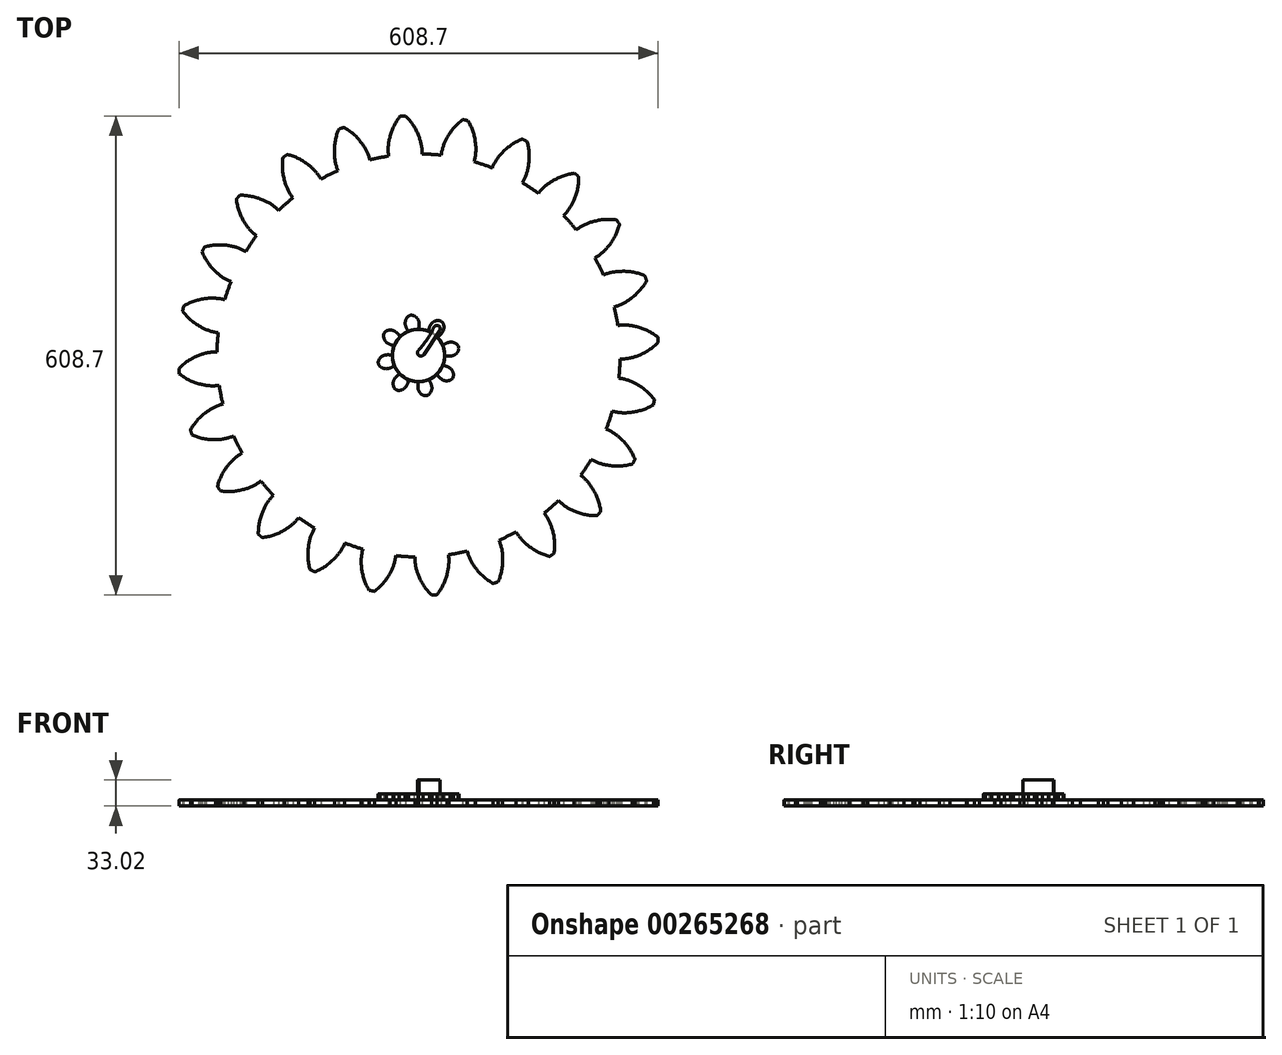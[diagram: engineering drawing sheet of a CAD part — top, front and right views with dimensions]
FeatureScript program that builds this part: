
annotation { "Feature Type Name" : "Feature", "Feature Type Description" : "" }
export const myFeature = defineFeature(function(context is Context, id is Id, definition is map)
    precondition{}
    {
        {
            var Q0;
            Q0=qCreatedBy(makeId("Top.planeOp"),FACE);
            var sketch = newSketch(context, id + "F0", { "sketchPlane" : qUnion([Q0])});
            skCircle(sketch, "E0", {"center": v(0, 0) * mm, "radius": 33.25 * mm});
            skCircle(sketch, "E1", {"center": v(0, 0) * mm, "radius": 44.32 * mm, "construction": true});
            skCircle(sketch, "E2", {"center": v(0, 0) * mm, "radius": 50.8 * mm, "construction": true});
            skLineSegment(sketch, "E3", {"start": v(0, 0) * mm, "end": v(0, 420.14) * mm, "construction": true});
            skLineSegment(sketch, "E4", {"start": v(0, 0) * mm, "end": v(-79.68, 400.58) * mm, "construction": true});
            skLineSegment(sketch, "E5", {"start": v(0, 44.32) * mm, "end": v(-381.83, 44.32) * mm, "construction": true});
            skLineSegment(sketch, "E6", {"start": v(0, 44.32) * mm, "end": v(-397.99, -100.53) * mm, "construction": true});
            skCircle(sketch, "E7", {"center": v(0, 0) * mm, "radius": 41.65 * mm, "construction": true});
            skCircle(sketch, "E8", {"center": v(0, 44.32) * mm, "radius": 11.08 * mm, "construction": true});
            skCircle(sketch, "E9", {"center": v(-10.35, 40.34) * mm, "radius": 69.82 * mm, "construction": true});
            skCircle(sketch, "E10", {"center": v(-10.35, 40.34) * mm, "radius": 11.08 * mm, "construction": true});
            skArc(sketch, "E11", {"start": v(0, 44.32) * mm, "mid": v(-2.33, 47.95) * mm, "end": v(-5.83, 50.46) * mm});
            skArc(sketch, "E12", {"start": v(0, 33.24) * mm, "mid": v(0.9, 38.78) * mm, "end": v(0, 44.32) * mm});
            skArc(sketch, "E13.MirrorCS", {"start": v(-12.72, 30.7) * mm, "mid": v(-15.67, 35.49) * mm, "end": v(-16.96, 40.95) * mm});
            skArc(sketch, "E14.MirrorCS", {"start": v(-16.96, 40.95) * mm, "mid": v(-16.2, 45.2) * mm, "end": v(-13.93, 48.85) * mm});
            skArc(sketch, "E15", {"start": v(-5.83, 50.46) * mm, "mid": v(-10.15, 51.04) * mm, "end": v(-13.93, 48.85) * mm});
            skSolve(sketch);
        }
        {
            var Q0;
            Q0=qSketchRegion(id+"F0",true);
            extrude(context, id + "F1", {"entities" : qUnion([Q0]), "depth" : 7.62 * mm});
        }
        {
            var Q0;
            Q0=makeQuery(id+"F1.opExtrude","SWEPT_BODY",BODY,{"disambiguationData":[OSD([sQuery(id+"F0.wireOp",EDGE,"E0"),sQuery(id+"F0.wireOp",EDGE,"91NiUCr4-yXFt-oEsC-2t8w-iLQuIMEs0WGp"),sQuery(id+"F0.wireOp",EDGE,"2eccd6a7-b62e-4e30-96b3-c5b5e07e5a5b0.MirrorCS"),sQuery(id+"F0.wireOp",EDGE,"SwGH1OBa-uFWg-PKz4-vmGh-Pag9Jd44Z9b1")])]});
            var Q1;
            Q1=makeQuery(id+"F1.opExtrude","SWEPT_FACE",FACE,{"disambiguationData":[OSD([sQuery(id+"F0.wireOp",EDGE,"E0")])]});
            circularPattern(context, id + "F2", {"entities" : qUnion([Q0]), "axis" : qUnion([Q1]), "angle" : 360 * degree, "instanceCount" : 8, "equalSpace" : true});
        }
        {
            var Q0;
            Q0=qCreatedBy(makeId("Top.planeOp"),FACE);
            var sketch = newSketch(context, id + "F3", { "sketchPlane" : qUnion([Q0])});
            skLineSegment(sketch, "E16", {"start": v(0, 0) * mm, "end": v(85.76, 128.36) * mm, "construction": true});
            skLineSegment(sketch, "E17.bottom", {"start": v(4.22, -2.82) * mm, "end": v(29.62, 35.2) * mm});
            skLineSegment(sketch, "E17.top", {"start": v(0, 0) * mm, "end": v(25.4, 38.01) * mm});
            skLineSegment(sketch, "E17.left", {"start": v(4.22, -2.82) * mm, "end": v(0, 0) * mm});
            skLineSegment(sketch, "E17.right", {"start": v(29.62, 35.2) * mm, "end": v(25.4, 38.01) * mm});
            skLineSegment(sketch, "E18.left", {"start": v(-4.22, 2.82) * mm, "end": v(0, 0) * mm});
            skLineSegment(sketch, "E18.right", {"start": v(21.18, 40.84) * mm, "end": v(25.4, 38.01) * mm});
            skArc(sketch, "E19", {"start": v(-4.22, 2.82) * mm, "mid": v(10.92, 20.2) * mm, "end": v(21.18, 40.84) * mm});
            skSolve(sketch);
        }
        {
            var Q0;
            Q0 = qSketchRegion(id + "F3", true);
            extrude(context, id + "F4", {"entities" : qUnion([Q0]), "depth" : 25.4 * mm});
        }
        {
            var Q0;
            Q0=makeQuery(id+"F4.opExtrude","SWEPT_EDGE",EDGE,{"disambiguationData":[OSD([sQuery(id+"F3.wireOp",EDGE,"E17.bottom"),sQuery(id+"F3.wireOp",EDGE,"E17.right")])]});
            var Q1;
            Q1=makeQuery(id+"F4.opExtrude","SWEPT_EDGE",EDGE,{"disambiguationData":[OSD([sQuery(id+"F3.wireOp",EDGE,"E17.bottom"),sQuery(id+"F3.wireOp",EDGE,"E17.left")])]});
            var Q2;
            Q2=makeQuery(id+"F4.opExtrude","SWEPT_EDGE",EDGE,{"disambiguationData":[OSD([sQuery(id+"F3.wireOp",EDGE,"E18.left"),sQuery(id+"F3.wireOp",EDGE,"E19")])]});
            var Q3;
            Q3=makeQuery(id+"F4.opExtrude","SWEPT_EDGE",EDGE,{"disambiguationData":[OSD([sQuery(id+"F3.wireOp",EDGE,"E18.right"),sQuery(id+"F3.wireOp",EDGE,"E19")])]});
            fillet(context, id + "F5", {"entities" : qUnion([Q0, Q1, Q2, Q3]), "radius" : 5.08 * mm, "tangentPropagation" : true, "allowEdgeOverflow" : false});
        }
        {
            var Q0;
            Q0=qCreatedBy(makeId("Top.planeOp"),FACE);
            var sketch = newSketch(context, id + "F6", { "sketchPlane" : qUnion([Q0])});
            skCircle(sketch, "E20", {"center": v(0, 0) * mm, "radius": 256.02 * mm});
            skCircle(sketch, "E21", {"center": v(0, 0) * mm, "radius": 279.3 * mm, "construction": true});
            skCircle(sketch, "E22", {"center": v(0, 0) * mm, "radius": 304.8 * mm, "construction": true});
            skLineSegment(sketch, "E23", {"start": v(0, 0) * mm, "end": v(0, 185.17) * mm, "construction": true});
            skLineSegment(sketch, "E24", {"start": v(0, 0) * mm, "end": v(-26.71, 407.56) * mm, "construction": true});
            skLineSegment(sketch, "E25", {"start": v(0, 279.3) * mm, "end": v(-381.83, 279.3) * mm, "construction": true});
            skLineSegment(sketch, "E26", {"start": v(0, 279.3) * mm, "end": v(-397.99, 134.44) * mm, "construction": true});
            skCircle(sketch, "E27", {"center": v(0, 0) * mm, "radius": 262.45 * mm, "construction": true});
            skCircle(sketch, "E28", {"center": v(0, 279.3) * mm, "radius": 69.82 * mm, "construction": true});
            skCircle(sketch, "E29", {"center": v(-65.17, 254.23) * mm, "radius": 69.82 * mm, "construction": true});
            skArc(sketch, "E30", {"start": v(-16.55, 304.35) * mm, "mid": v(-19.94, 304.2) * mm, "end": v(-23.32, 303.9) * mm});
            skArc(sketch, "E31", {"start": v(0, 279.3) * mm, "mid": v(-6.88, 292.75) * mm, "end": v(-16.55, 304.35) * mm});
            skArc(sketch, "E32.MirrorCS", {"start": v(-36.46, 276.9) * mm, "mid": v(-31.4, 291.14) * mm, "end": v(-23.32, 303.9) * mm});
            skArc(sketch, "E33", {"start": v(-36.46, 276.9) * mm, "mid": v(-38.45, 265.13) * mm, "end": v(-38, 253.19) * mm});
            skArc(sketch, "E34.MirrorCS", {"start": v(0, 279.3) * mm, "mid": v(3.51, 267.88) * mm, "end": v(4.63, 255.98) * mm});
            skSolve(sketch);
        }
        {
            var Q0;
            Q0 = qSketchRegion(id + "F6", true);
            extrude(context, id + "F7", {"entities" : qUnion([Q0]), "depth" : 7.62 * mm});
        }
        {
            var Q0;
            Q0=makeQuery(id+"F7.opExtrude","SWEPT_BODY",BODY,{"disambiguationData":[OSD([sQuery(id+"F6.wireOp",EDGE,"E20"),sQuery(id+"F6.wireOp",EDGE,"E30"),sQuery(id+"F6.wireOp",EDGE,"E31"),sQuery(id+"F6.wireOp",EDGE,"E32.MirrorCS"),sQuery(id+"F6.wireOp",EDGE,"E33"),sQuery(id+"F6.wireOp",EDGE,"E34.MirrorCS")])]});
            var Q1;
            Q1=makeQuery(id+"F7.opExtrude","SWEPT_FACE",FACE,{"disambiguationData":[OSD([sQuery(id+"F6.wireOp",EDGE,"E20")])]});
            circularPattern(context, id + "F8", {"entities" : qUnion([Q0]), "axis" : qUnion([Q1]), "angle" : 360 * degree, "instanceCount" : 24, "equalSpace" : true});
        }
        {
            var Q0;
            Q0=makeQuery(id+"F7.opExtrude","SWEPT_BODY",BODY,{"disambiguationData":[OSD([sQuery(id+"F6.wireOp",EDGE,"E20"),sQuery(id+"F6.wireOp",EDGE,"E30"),sQuery(id+"F6.wireOp",EDGE,"E31"),sQuery(id+"F6.wireOp",EDGE,"E32.MirrorCS"),sQuery(id+"F6.wireOp",EDGE,"E33"),sQuery(id+"F6.wireOp",EDGE,"E34.MirrorCS")])]});
            var Q1;
            Q1=makeQuery(id+"F8.opPattern","COPY",BODY,{"derivedFrom":makeQuery(id+"F7.opExtrude","SWEPT_BODY",BODY,{"disambiguationData":[OSD([sQuery(id+"F6.wireOp",EDGE,"E20"),sQuery(id+"F6.wireOp",EDGE,"E30"),sQuery(id+"F6.wireOp",EDGE,"E31"),sQuery(id+"F6.wireOp",EDGE,"E32.MirrorCS"),sQuery(id+"F6.wireOp",EDGE,"E33"),sQuery(id+"F6.wireOp",EDGE,"E34.MirrorCS")])]}),"instanceName":"1"});
            var Q2;
            Q2=makeQuery(id+"F8.opPattern","COPY",BODY,{"derivedFrom":makeQuery(id+"F7.opExtrude","SWEPT_BODY",BODY,{"disambiguationData":[OSD([sQuery(id+"F6.wireOp",EDGE,"E20"),sQuery(id+"F6.wireOp",EDGE,"E30"),sQuery(id+"F6.wireOp",EDGE,"E31"),sQuery(id+"F6.wireOp",EDGE,"E32.MirrorCS"),sQuery(id+"F6.wireOp",EDGE,"E33"),sQuery(id+"F6.wireOp",EDGE,"E34.MirrorCS")])]}),"instanceName":"2"});
            var Q3;
            Q3=makeQuery(id+"F8.opPattern","COPY",BODY,{"derivedFrom":makeQuery(id+"F7.opExtrude","SWEPT_BODY",BODY,{"disambiguationData":[OSD([sQuery(id+"F6.wireOp",EDGE,"E20"),sQuery(id+"F6.wireOp",EDGE,"E30"),sQuery(id+"F6.wireOp",EDGE,"E31"),sQuery(id+"F6.wireOp",EDGE,"E32.MirrorCS"),sQuery(id+"F6.wireOp",EDGE,"E33"),sQuery(id+"F6.wireOp",EDGE,"E34.MirrorCS")])]}),"instanceName":"3"});
            var Q4;
            Q4=makeQuery(id+"F8.opPattern","COPY",BODY,{"derivedFrom":makeQuery(id+"F7.opExtrude","SWEPT_BODY",BODY,{"disambiguationData":[OSD([sQuery(id+"F6.wireOp",EDGE,"E20"),sQuery(id+"F6.wireOp",EDGE,"E30"),sQuery(id+"F6.wireOp",EDGE,"E31"),sQuery(id+"F6.wireOp",EDGE,"E32.MirrorCS"),sQuery(id+"F6.wireOp",EDGE,"E33"),sQuery(id+"F6.wireOp",EDGE,"E34.MirrorCS")])]}),"instanceName":"4"});
            var Q5;
            Q5=makeQuery(id+"F8.opPattern","COPY",BODY,{"derivedFrom":makeQuery(id+"F7.opExtrude","SWEPT_BODY",BODY,{"disambiguationData":[OSD([sQuery(id+"F6.wireOp",EDGE,"E20"),sQuery(id+"F6.wireOp",EDGE,"E30"),sQuery(id+"F6.wireOp",EDGE,"E31"),sQuery(id+"F6.wireOp",EDGE,"E32.MirrorCS"),sQuery(id+"F6.wireOp",EDGE,"E33"),sQuery(id+"F6.wireOp",EDGE,"E34.MirrorCS")])]}),"instanceName":"5"});
            var Q6;
            Q6=makeQuery(id+"F8.opPattern","COPY",BODY,{"derivedFrom":makeQuery(id+"F7.opExtrude","SWEPT_BODY",BODY,{"disambiguationData":[OSD([sQuery(id+"F6.wireOp",EDGE,"E20"),sQuery(id+"F6.wireOp",EDGE,"E30"),sQuery(id+"F6.wireOp",EDGE,"E31"),sQuery(id+"F6.wireOp",EDGE,"E32.MirrorCS"),sQuery(id+"F6.wireOp",EDGE,"E33"),sQuery(id+"F6.wireOp",EDGE,"E34.MirrorCS")])]}),"instanceName":"6"});
            var Q7;
            Q7=makeQuery(id+"F8.opPattern","COPY",BODY,{"derivedFrom":makeQuery(id+"F7.opExtrude","SWEPT_BODY",BODY,{"disambiguationData":[OSD([sQuery(id+"F6.wireOp",EDGE,"E20"),sQuery(id+"F6.wireOp",EDGE,"E30"),sQuery(id+"F6.wireOp",EDGE,"E31"),sQuery(id+"F6.wireOp",EDGE,"E32.MirrorCS"),sQuery(id+"F6.wireOp",EDGE,"E33"),sQuery(id+"F6.wireOp",EDGE,"E34.MirrorCS")])]}),"instanceName":"7"});
            var Q8;
            Q8=makeQuery(id+"F8.opPattern","COPY",BODY,{"derivedFrom":makeQuery(id+"F7.opExtrude","SWEPT_BODY",BODY,{"disambiguationData":[OSD([sQuery(id+"F6.wireOp",EDGE,"E20"),sQuery(id+"F6.wireOp",EDGE,"E30"),sQuery(id+"F6.wireOp",EDGE,"E31"),sQuery(id+"F6.wireOp",EDGE,"E32.MirrorCS"),sQuery(id+"F6.wireOp",EDGE,"E33"),sQuery(id+"F6.wireOp",EDGE,"E34.MirrorCS")])]}),"instanceName":"8"});
            var Q9;
            Q9=makeQuery(id+"F8.opPattern","COPY",BODY,{"derivedFrom":makeQuery(id+"F7.opExtrude","SWEPT_BODY",BODY,{"disambiguationData":[OSD([sQuery(id+"F6.wireOp",EDGE,"E20"),sQuery(id+"F6.wireOp",EDGE,"E30"),sQuery(id+"F6.wireOp",EDGE,"E31"),sQuery(id+"F6.wireOp",EDGE,"E32.MirrorCS"),sQuery(id+"F6.wireOp",EDGE,"E33"),sQuery(id+"F6.wireOp",EDGE,"E34.MirrorCS")])]}),"instanceName":"9"});
            var Q10;
            Q10=makeQuery(id+"F8.opPattern","COPY",BODY,{"derivedFrom":makeQuery(id+"F7.opExtrude","SWEPT_BODY",BODY,{"disambiguationData":[OSD([sQuery(id+"F6.wireOp",EDGE,"E20"),sQuery(id+"F6.wireOp",EDGE,"E30"),sQuery(id+"F6.wireOp",EDGE,"E31"),sQuery(id+"F6.wireOp",EDGE,"E32.MirrorCS"),sQuery(id+"F6.wireOp",EDGE,"E33"),sQuery(id+"F6.wireOp",EDGE,"E34.MirrorCS")])]}),"instanceName":"10"});
            var Q11;
            Q11=makeQuery(id+"F8.opPattern","COPY",BODY,{"derivedFrom":makeQuery(id+"F7.opExtrude","SWEPT_BODY",BODY,{"disambiguationData":[OSD([sQuery(id+"F6.wireOp",EDGE,"E20"),sQuery(id+"F6.wireOp",EDGE,"E30"),sQuery(id+"F6.wireOp",EDGE,"E31"),sQuery(id+"F6.wireOp",EDGE,"E32.MirrorCS"),sQuery(id+"F6.wireOp",EDGE,"E33"),sQuery(id+"F6.wireOp",EDGE,"E34.MirrorCS")])]}),"instanceName":"11"});
            var Q12;
            Q12=makeQuery(id+"F8.opPattern","COPY",BODY,{"derivedFrom":makeQuery(id+"F7.opExtrude","SWEPT_BODY",BODY,{"disambiguationData":[OSD([sQuery(id+"F6.wireOp",EDGE,"E20"),sQuery(id+"F6.wireOp",EDGE,"E30"),sQuery(id+"F6.wireOp",EDGE,"E31"),sQuery(id+"F6.wireOp",EDGE,"E32.MirrorCS"),sQuery(id+"F6.wireOp",EDGE,"E33"),sQuery(id+"F6.wireOp",EDGE,"E34.MirrorCS")])]}),"instanceName":"12"});
            var Q13;
            Q13=makeQuery(id+"F8.opPattern","COPY",BODY,{"derivedFrom":makeQuery(id+"F7.opExtrude","SWEPT_BODY",BODY,{"disambiguationData":[OSD([sQuery(id+"F6.wireOp",EDGE,"E20"),sQuery(id+"F6.wireOp",EDGE,"E30"),sQuery(id+"F6.wireOp",EDGE,"E31"),sQuery(id+"F6.wireOp",EDGE,"E32.MirrorCS"),sQuery(id+"F6.wireOp",EDGE,"E33"),sQuery(id+"F6.wireOp",EDGE,"E34.MirrorCS")])]}),"instanceName":"13"});
            var Q14;
            Q14=makeQuery(id+"F8.opPattern","COPY",BODY,{"derivedFrom":makeQuery(id+"F7.opExtrude","SWEPT_BODY",BODY,{"disambiguationData":[OSD([sQuery(id+"F6.wireOp",EDGE,"E20"),sQuery(id+"F6.wireOp",EDGE,"E30"),sQuery(id+"F6.wireOp",EDGE,"E31"),sQuery(id+"F6.wireOp",EDGE,"E32.MirrorCS"),sQuery(id+"F6.wireOp",EDGE,"E33"),sQuery(id+"F6.wireOp",EDGE,"E34.MirrorCS")])]}),"instanceName":"14"});
            var Q15;
            Q15=makeQuery(id+"F8.opPattern","COPY",BODY,{"derivedFrom":makeQuery(id+"F7.opExtrude","SWEPT_BODY",BODY,{"disambiguationData":[OSD([sQuery(id+"F6.wireOp",EDGE,"E20"),sQuery(id+"F6.wireOp",EDGE,"E30"),sQuery(id+"F6.wireOp",EDGE,"E31"),sQuery(id+"F6.wireOp",EDGE,"E32.MirrorCS"),sQuery(id+"F6.wireOp",EDGE,"E33"),sQuery(id+"F6.wireOp",EDGE,"E34.MirrorCS")])]}),"instanceName":"15"});
            var Q16;
            Q16=makeQuery(id+"F8.opPattern","COPY",BODY,{"derivedFrom":makeQuery(id+"F7.opExtrude","SWEPT_BODY",BODY,{"disambiguationData":[OSD([sQuery(id+"F6.wireOp",EDGE,"E20"),sQuery(id+"F6.wireOp",EDGE,"E30"),sQuery(id+"F6.wireOp",EDGE,"E31"),sQuery(id+"F6.wireOp",EDGE,"E32.MirrorCS"),sQuery(id+"F6.wireOp",EDGE,"E33"),sQuery(id+"F6.wireOp",EDGE,"E34.MirrorCS")])]}),"instanceName":"16"});
            var Q17;
            Q17=makeQuery(id+"F8.opPattern","COPY",BODY,{"derivedFrom":makeQuery(id+"F7.opExtrude","SWEPT_BODY",BODY,{"disambiguationData":[OSD([sQuery(id+"F6.wireOp",EDGE,"E20"),sQuery(id+"F6.wireOp",EDGE,"E30"),sQuery(id+"F6.wireOp",EDGE,"E31"),sQuery(id+"F6.wireOp",EDGE,"E32.MirrorCS"),sQuery(id+"F6.wireOp",EDGE,"E33"),sQuery(id+"F6.wireOp",EDGE,"E34.MirrorCS")])]}),"instanceName":"17"});
            var Q18;
            Q18=makeQuery(id+"F8.opPattern","COPY",BODY,{"derivedFrom":makeQuery(id+"F7.opExtrude","SWEPT_BODY",BODY,{"disambiguationData":[OSD([sQuery(id+"F6.wireOp",EDGE,"E20"),sQuery(id+"F6.wireOp",EDGE,"E30"),sQuery(id+"F6.wireOp",EDGE,"E31"),sQuery(id+"F6.wireOp",EDGE,"E32.MirrorCS"),sQuery(id+"F6.wireOp",EDGE,"E33"),sQuery(id+"F6.wireOp",EDGE,"E34.MirrorCS")])]}),"instanceName":"18"});
            var Q19;
            Q19=makeQuery(id+"F8.opPattern","COPY",BODY,{"derivedFrom":makeQuery(id+"F7.opExtrude","SWEPT_BODY",BODY,{"disambiguationData":[OSD([sQuery(id+"F6.wireOp",EDGE,"E20"),sQuery(id+"F6.wireOp",EDGE,"E30"),sQuery(id+"F6.wireOp",EDGE,"E31"),sQuery(id+"F6.wireOp",EDGE,"E32.MirrorCS"),sQuery(id+"F6.wireOp",EDGE,"E33"),sQuery(id+"F6.wireOp",EDGE,"E34.MirrorCS")])]}),"instanceName":"19"});
            var Q20;
            Q20=makeQuery(id+"F8.opPattern","COPY",BODY,{"derivedFrom":makeQuery(id+"F7.opExtrude","SWEPT_BODY",BODY,{"disambiguationData":[OSD([sQuery(id+"F6.wireOp",EDGE,"E20"),sQuery(id+"F6.wireOp",EDGE,"E30"),sQuery(id+"F6.wireOp",EDGE,"E31"),sQuery(id+"F6.wireOp",EDGE,"E32.MirrorCS"),sQuery(id+"F6.wireOp",EDGE,"E33"),sQuery(id+"F6.wireOp",EDGE,"E34.MirrorCS")])]}),"instanceName":"20"});
            var Q21;
            Q21=makeQuery(id+"F8.opPattern","COPY",BODY,{"derivedFrom":makeQuery(id+"F7.opExtrude","SWEPT_BODY",BODY,{"disambiguationData":[OSD([sQuery(id+"F6.wireOp",EDGE,"E20"),sQuery(id+"F6.wireOp",EDGE,"E30"),sQuery(id+"F6.wireOp",EDGE,"E31"),sQuery(id+"F6.wireOp",EDGE,"E32.MirrorCS"),sQuery(id+"F6.wireOp",EDGE,"E33"),sQuery(id+"F6.wireOp",EDGE,"E34.MirrorCS")])]}),"instanceName":"21"});
            var Q22;
            Q22=makeQuery(id+"F8.opPattern","COPY",BODY,{"derivedFrom":makeQuery(id+"F7.opExtrude","SWEPT_BODY",BODY,{"disambiguationData":[OSD([sQuery(id+"F6.wireOp",EDGE,"E20"),sQuery(id+"F6.wireOp",EDGE,"E30"),sQuery(id+"F6.wireOp",EDGE,"E31"),sQuery(id+"F6.wireOp",EDGE,"E32.MirrorCS"),sQuery(id+"F6.wireOp",EDGE,"E33"),sQuery(id+"F6.wireOp",EDGE,"E34.MirrorCS")])]}),"instanceName":"22"});
            var Q23;
            Q23=makeQuery(id+"F8.opPattern","COPY",BODY,{"derivedFrom":makeQuery(id+"F7.opExtrude","SWEPT_BODY",BODY,{"disambiguationData":[OSD([sQuery(id+"F6.wireOp",EDGE,"E20"),sQuery(id+"F6.wireOp",EDGE,"E30"),sQuery(id+"F6.wireOp",EDGE,"E31"),sQuery(id+"F6.wireOp",EDGE,"E32.MirrorCS"),sQuery(id+"F6.wireOp",EDGE,"E33"),sQuery(id+"F6.wireOp",EDGE,"E34.MirrorCS")])]}),"instanceName":"23"});
            booleanBodies(context, id + "F9", {"operationType" : BooleanOperationType.UNION, "tools" : qUnion([Q0, Q1, Q2, Q3, Q4, Q5, Q6, Q7, Q8, Q9, Q10, Q11, Q12, Q13, Q14, Q15, Q16, Q17, Q18, Q19, Q20, Q21, Q22, Q23])});
        }
        {
            var Q0;
            Q0=makeQuery(id+"F7.opExtrude","SWEPT_BODY",BODY,{"disambiguationData":[OSD([sQuery(id+"F6.wireOp",EDGE,"E20"),sQuery(id+"F6.wireOp",EDGE,"E30"),sQuery(id+"F6.wireOp",EDGE,"E31"),sQuery(id+"F6.wireOp",EDGE,"E32.MirrorCS"),sQuery(id+"F6.wireOp",EDGE,"E33"),sQuery(id+"F6.wireOp",EDGE,"E34.MirrorCS")])]});
            transform(context, id + "F10", {"entities" : qUnion([Q0]), "transformType" : TransformType.TRANSLATION_3D, "dx" : 0 * mm, "dy" : 0 * mm, "dz" : -7.62 * mm, "makeCopy" : false});
        }
        {
            var Q0;
            {var subQ0=makeQuery(id+"F7.opExtrude","CAP_FACE",FACE,{"disambiguationData":[OSD([sQuery(id+"F6.wireOp",EDGE,"E20"),sQuery(id+"F6.wireOp",EDGE,"E30"),sQuery(id+"F6.wireOp",EDGE,"E31"),sQuery(id+"F6.wireOp",EDGE,"E32.MirrorCS"),sQuery(id+"F6.wireOp",EDGE,"E33"),sQuery(id+"F6.wireOp",EDGE,"E34.MirrorCS")])],"isStart":false});Q0=makeQuery(id+"F9.opBoolean","MERGE",FACE,{"derivedFrom":[subQ0,makeQuery(id+"F8.opPattern","COPY",FACE,{"derivedFrom":subQ0,"instanceName":"1"}),makeQuery(id+"F8.opPattern","COPY",FACE,{"derivedFrom":subQ0,"instanceName":"2"}),makeQuery(id+"F8.opPattern","COPY",FACE,{"derivedFrom":subQ0,"instanceName":"3"}),makeQuery(id+"F8.opPattern","COPY",FACE,{"derivedFrom":subQ0,"instanceName":"4"}),makeQuery(id+"F8.opPattern","COPY",FACE,{"derivedFrom":subQ0,"instanceName":"5"}),makeQuery(id+"F8.opPattern","COPY",FACE,{"derivedFrom":subQ0,"instanceName":"6"}),makeQuery(id+"F8.opPattern","COPY",FACE,{"derivedFrom":subQ0,"instanceName":"7"}),makeQuery(id+"F8.opPattern","COPY",FACE,{"derivedFrom":subQ0,"instanceName":"8"}),makeQuery(id+"F8.opPattern","COPY",FACE,{"derivedFrom":subQ0,"instanceName":"9"}),makeQuery(id+"F8.opPattern","COPY",FACE,{"derivedFrom":subQ0,"instanceName":"10"}),makeQuery(id+"F8.opPattern","COPY",FACE,{"derivedFrom":subQ0,"instanceName":"11"}),makeQuery(id+"F8.opPattern","COPY",FACE,{"derivedFrom":subQ0,"instanceName":"12"}),makeQuery(id+"F8.opPattern","COPY",FACE,{"derivedFrom":subQ0,"instanceName":"13"}),makeQuery(id+"F8.opPattern","COPY",FACE,{"derivedFrom":subQ0,"instanceName":"14"}),makeQuery(id+"F8.opPattern","COPY",FACE,{"derivedFrom":subQ0,"instanceName":"15"}),makeQuery(id+"F8.opPattern","COPY",FACE,{"derivedFrom":subQ0,"instanceName":"16"}),makeQuery(id+"F8.opPattern","COPY",FACE,{"derivedFrom":subQ0,"instanceName":"17"}),makeQuery(id+"F8.opPattern","COPY",FACE,{"derivedFrom":subQ0,"instanceName":"18"}),makeQuery(id+"F8.opPattern","COPY",FACE,{"derivedFrom":subQ0,"instanceName":"19"}),makeQuery(id+"F8.opPattern","COPY",FACE,{"derivedFrom":subQ0,"instanceName":"20"}),makeQuery(id+"F8.opPattern","COPY",FACE,{"derivedFrom":subQ0,"instanceName":"21"}),makeQuery(id+"F8.opPattern","COPY",FACE,{"derivedFrom":subQ0,"instanceName":"22"}),makeQuery(id+"F8.opPattern","COPY",FACE,{"derivedFrom":subQ0,"instanceName":"23"})]});}
            var sketch = newSketch(context, id + "F11", { "sketchPlane" : qUnion([Q0])});
            skLineSegment(sketch, "E35", {"start": v(0, 0) * mm, "end": v(200.97, 229.16) * mm, "construction": true});
            skCircle(sketch, "E36", {"center": v(100.48, 114.58) * mm, "radius": 63.5 * mm});
            skSolve(sketch);
        }
        {
            var Q0;
            Q0=makeQuery(id+"F11.imprint","IMPRINT",FACE,{"disambiguationData":[TD([[makeQuery(id+"F11.imprint","IMPRINT",EDGE,{"derivedFrom":sQuery(id+"F11.wireOp",EDGE,"E36")}),1.0]])]});
            extrude(context, id + "F12", {"entities" : qUnion([Q0]), "oppositeDirection" : true, "depth" : 25.4 * mm});
        }
        {
            var Q0;
            Q0=makeQuery(id+"F12.opExtrude","SWEPT_BODY",BODY,{"disambiguationData":[OSD([sQuery(id+"F11.wireOp",EDGE,"E36")])]});
            var Q1;
            Q1=sQuery(id+"F6.wireOp",EDGE,"E20");
            circularPattern(context, id + "F13", {"entities" : qUnion([Q0]), "axis" : qUnion([Q1]), "angle" : 360 * degree, "instanceCount" : 6, "equalSpace" : true});
        }
        {
            var Q0;
            Q0=makeQuery(id+"F12.opExtrude","SWEPT_BODY",BODY,{"disambiguationData":[OSD([sQuery(id+"F11.wireOp",EDGE,"E36")])]});
            var Q1;
            Q1=makeQuery(id+"F13.opPattern","COPY",BODY,{"derivedFrom":makeQuery(id+"F12.opExtrude","SWEPT_BODY",BODY,{"disambiguationData":[OSD([sQuery(id+"F11.wireOp",EDGE,"E36")])]}),"instanceName":"1"});
            var Q2;
            Q2=makeQuery(id+"F13.opPattern","COPY",BODY,{"derivedFrom":makeQuery(id+"F12.opExtrude","SWEPT_BODY",BODY,{"disambiguationData":[OSD([sQuery(id+"F11.wireOp",EDGE,"E36")])]}),"instanceName":"2"});
            var Q3;
            Q3=makeQuery(id+"F13.opPattern","COPY",BODY,{"derivedFrom":makeQuery(id+"F12.opExtrude","SWEPT_BODY",BODY,{"disambiguationData":[OSD([sQuery(id+"F11.wireOp",EDGE,"E36")])]}),"instanceName":"3"});
            var Q4;
            Q4=makeQuery(id+"F13.opPattern","COPY",BODY,{"derivedFrom":makeQuery(id+"F12.opExtrude","SWEPT_BODY",BODY,{"disambiguationData":[OSD([sQuery(id+"F11.wireOp",EDGE,"E36")])]}),"instanceName":"4"});
            var Q5;
            Q5=makeQuery(id+"F13.opPattern","COPY",BODY,{"derivedFrom":makeQuery(id+"F12.opExtrude","SWEPT_BODY",BODY,{"disambiguationData":[OSD([sQuery(id+"F11.wireOp",EDGE,"E36")])]}),"instanceName":"5"});
            var Q6;
            Q6=makeQuery(id+"F1.opExtrude","SWEPT_BODY",BODY,{"disambiguationData":[OSD([sQuery(id+"F0.wireOp",EDGE,"E0"),sQuery(id+"F0.wireOp",EDGE,"E11"),sQuery(id+"F0.wireOp",EDGE,"E12"),sQuery(id+"F0.wireOp",EDGE,"E13.MirrorCS"),sQuery(id+"F0.wireOp",EDGE,"E14.MirrorCS"),sQuery(id+"F0.wireOp",EDGE,"E15")])]});
            booleanBodies(context, id + "F14", {"operationType" : BooleanOperationType.SUBTRACTION, "tools" : qUnion([Q0, Q1, Q2, Q3, Q4, Q5]), "targets" : qUnion([Q6])});
        }
    });
